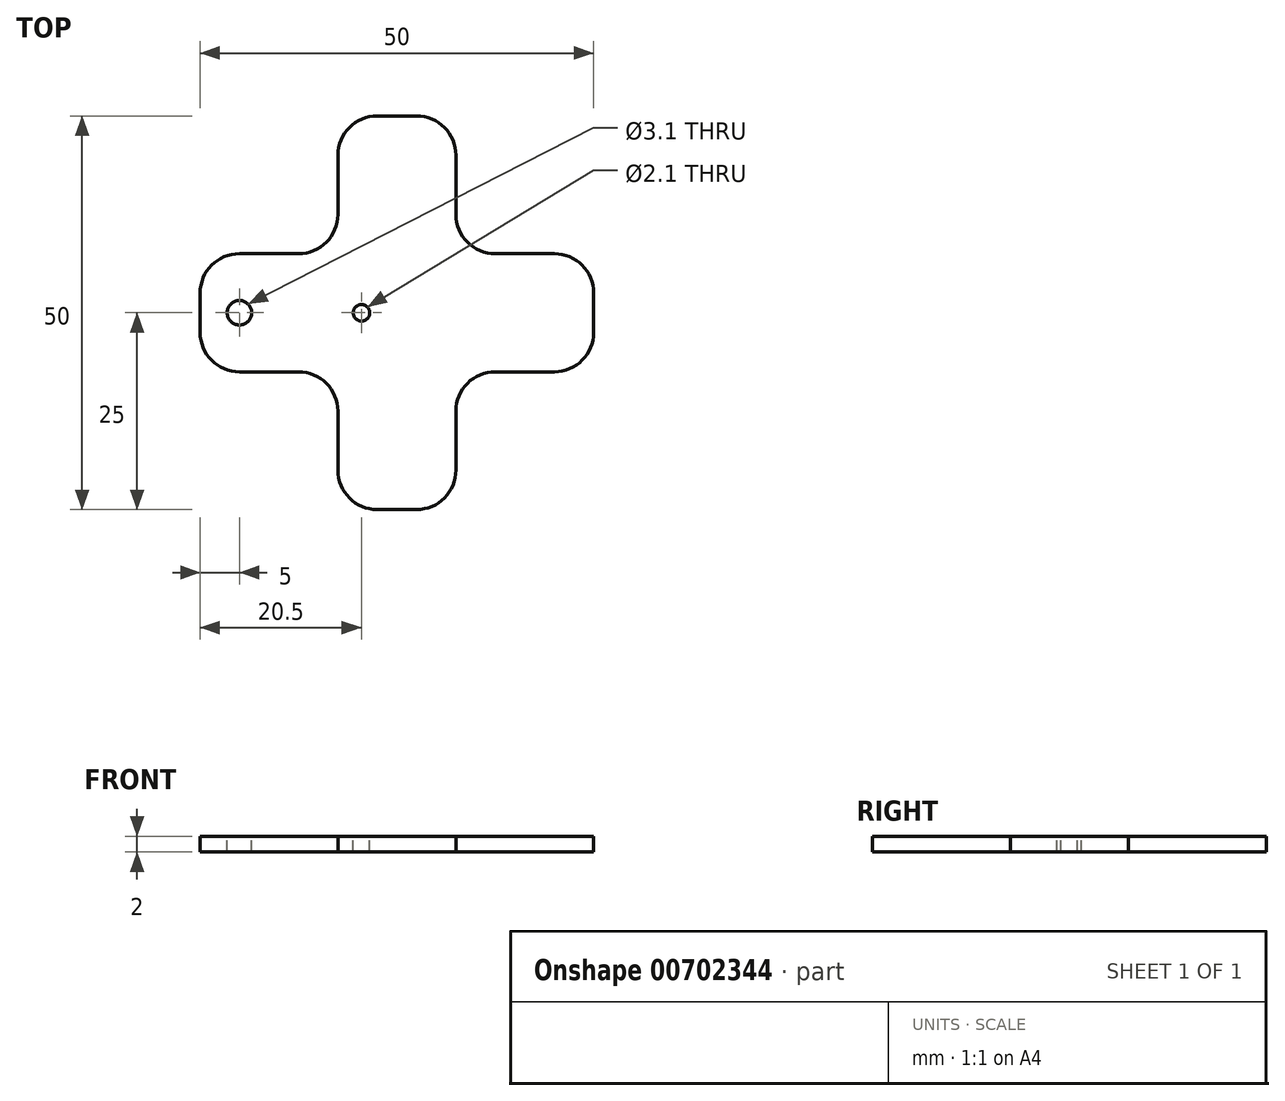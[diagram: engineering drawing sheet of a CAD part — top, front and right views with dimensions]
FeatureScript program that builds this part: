
annotation { "Feature Type Name" : "Feature", "Feature Type Description" : "" }
export const myFeature = defineFeature(function(context is Context, id is Id, definition is map)
    precondition{}
    {
        {
            var Q0;
            Q0=qCreatedBy(makeId("Top.planeOp"),FACE);
            var sketch = newSketch(context, id + "F0", { "sketchPlane" : qUnion([Q0])});
            skLineSegment(sketch, "E0.bottom", {"start": v(-7.5, 25) * mm, "end": v(7.5, 25) * mm});
            skLineSegment(sketch, "E0.top", {"start": v(-7.5, -25) * mm, "end": v(7.5, -25) * mm});
            skLineSegment(sketch, "E0.left", {"start": v(-7.5, 25) * mm, "end": v(-7.5, -25) * mm});
            skLineSegment(sketch, "E0.right", {"start": v(7.5, 25) * mm, "end": v(7.5, -25) * mm});
            skPoint(sketch, "E0.middle", {"position": v(0, 0) * mm});
            skLineSegment(sketch, "E1.bottom", {"start": v(-25, -7.5) * mm, "end": v(25, -7.5) * mm});
            skLineSegment(sketch, "E1.top", {"start": v(-25, 7.5) * mm, "end": v(25, 7.5) * mm});
            skLineSegment(sketch, "E1.left", {"start": v(-25, -7.5) * mm, "end": v(-25, 7.5) * mm});
            skLineSegment(sketch, "E1.right", {"start": v(25, -7.5) * mm, "end": v(25, 7.5) * mm});
            skSolve(sketch);
        }
        {
            var Q0;
            Q0 = qSketchRegion(id + "F0", true);
            extrude(context, id + "F1", {"entities" : qUnion([Q0]), "depth" : 2 * mm, "offsetDistance" : 25 * mm});
        }
        {
            var Q0;
            Q0=makeQuery(id+"F1.opExtrude","CAP_FACE",FACE,{"disambiguationData":[OSD([sQuery(id+"F0.wireOp",EDGE,"E0.bottom"),sQuery(id+"F0.wireOp",EDGE,"E0.top"),sQuery(id+"F0.wireOp",EDGE,"E0.left"),sQuery(id+"F0.wireOp",EDGE,"E0.right"),sQuery(id+"F0.wireOp",EDGE,"E1.bottom"),sQuery(id+"F0.wireOp",EDGE,"E1.top"),sQuery(id+"F0.wireOp",EDGE,"E1.left"),sQuery(id+"F0.wireOp",EDGE,"E1.right")])],"isStart":false});
            var sketch = newSketch(context, id + "F2", { "sketchPlane" : qUnion([Q0])});
            skCircle(sketch, "E2", {"center": v(0, 0) * mm, "radius": 4.5 * mm, "construction": true});
            skCircle(sketch, "E3", {"center": v(0, 0) * mm, "radius": 20 * mm, "construction": true});
            skCircle(sketch, "E4", {"center": v(-4.5, 0) * mm, "radius": 1.05 * mm});
            skCircle(sketch, "E5", {"center": v(-20, 0) * mm, "radius": 1.55 * mm});
            skSolve(sketch);
        }
        {
            var Q0;
            Q0 = qSketchRegion(id + "F2", true);
            extrude(context, id + "F3", {"entities" : qUnion([Q0]), "operationType" : NewBodyOperationType.REMOVE, "oppositeDirection" : true, "depth" : 25 * mm, "offsetDistance" : 25 * mm});
        }
        {
            var Q0;
            Q0=makeQuery(id+"F1.opExtrude","SWEPT_EDGE",EDGE,{"disambiguationData":[OSD([sQuery(id+"F0.wireOp",EDGE,"E0.top"),sQuery(id+"F0.wireOp",EDGE,"E0.right")])]});
            var Q1;
            Q1=makeQuery(id+"F1.opExtrude","SWEPT_EDGE",EDGE,{"disambiguationData":[OSD([sQuery(id+"F0.wireOp",EDGE,"E0.top"),sQuery(id+"F0.wireOp",EDGE,"E0.left")])]});
            var Q2;
            Q2=makeQuery(id+"F1.opExtrude","SWEPT_EDGE",EDGE,{"disambiguationData":[OSD([sQuery(id+"F0.wireOp",EDGE,"E0.left"),sQuery(id+"F0.wireOp",EDGE,"E1.bottom")])]});
            var Q3;
            Q3=makeQuery(id+"F1.opExtrude","SWEPT_EDGE",EDGE,{"disambiguationData":[OSD([sQuery(id+"F0.wireOp",EDGE,"E1.bottom"),sQuery(id+"F0.wireOp",EDGE,"E1.left")])]});
            var Q4;
            Q4=makeQuery(id+"F1.opExtrude","SWEPT_EDGE",EDGE,{"disambiguationData":[OSD([sQuery(id+"F0.wireOp",EDGE,"E1.top"),sQuery(id+"F0.wireOp",EDGE,"E1.left")])]});
            var Q5;
            Q5=makeQuery(id+"F1.opExtrude","SWEPT_EDGE",EDGE,{"disambiguationData":[OSD([sQuery(id+"F0.wireOp",EDGE,"E0.left"),sQuery(id+"F0.wireOp",EDGE,"E1.top")])]});
            var Q6;
            Q6=makeQuery(id+"F1.opExtrude","SWEPT_EDGE",EDGE,{"disambiguationData":[OSD([sQuery(id+"F0.wireOp",EDGE,"E0.bottom"),sQuery(id+"F0.wireOp",EDGE,"E0.left")])]});
            var Q7;
            Q7=makeQuery(id+"F1.opExtrude","SWEPT_EDGE",EDGE,{"disambiguationData":[OSD([sQuery(id+"F0.wireOp",EDGE,"E0.bottom"),sQuery(id+"F0.wireOp",EDGE,"E0.right")])]});
            var Q8;
            Q8=makeQuery(id+"F1.opExtrude","SWEPT_EDGE",EDGE,{"disambiguationData":[OSD([sQuery(id+"F0.wireOp",EDGE,"E1.top"),sQuery(id+"F0.wireOp",EDGE,"E1.right")])]});
            var Q9;
            Q9=makeQuery(id+"F1.opExtrude","SWEPT_EDGE",EDGE,{"disambiguationData":[OSD([sQuery(id+"F0.wireOp",EDGE,"E0.right"),sQuery(id+"F0.wireOp",EDGE,"E1.top")])]});
            var Q10;
            Q10=makeQuery(id+"F1.opExtrude","SWEPT_EDGE",EDGE,{"disambiguationData":[OSD([sQuery(id+"F0.wireOp",EDGE,"E1.bottom"),sQuery(id+"F0.wireOp",EDGE,"E1.right")])]});
            var Q11;
            Q11=makeQuery(id+"F1.opExtrude","SWEPT_EDGE",EDGE,{"disambiguationData":[OSD([sQuery(id+"F0.wireOp",EDGE,"E0.right"),sQuery(id+"F0.wireOp",EDGE,"E1.bottom")])]});
            fillet(context, id + "F4", {"entities" : qUnion([Q0, Q1, Q2, Q3, Q4, Q5, Q6, Q7, Q8, Q9, Q10, Q11]), "radius" : 5 * mm, "tangentPropagation" : true, "allowEdgeOverflow" : false});
        }
    });
